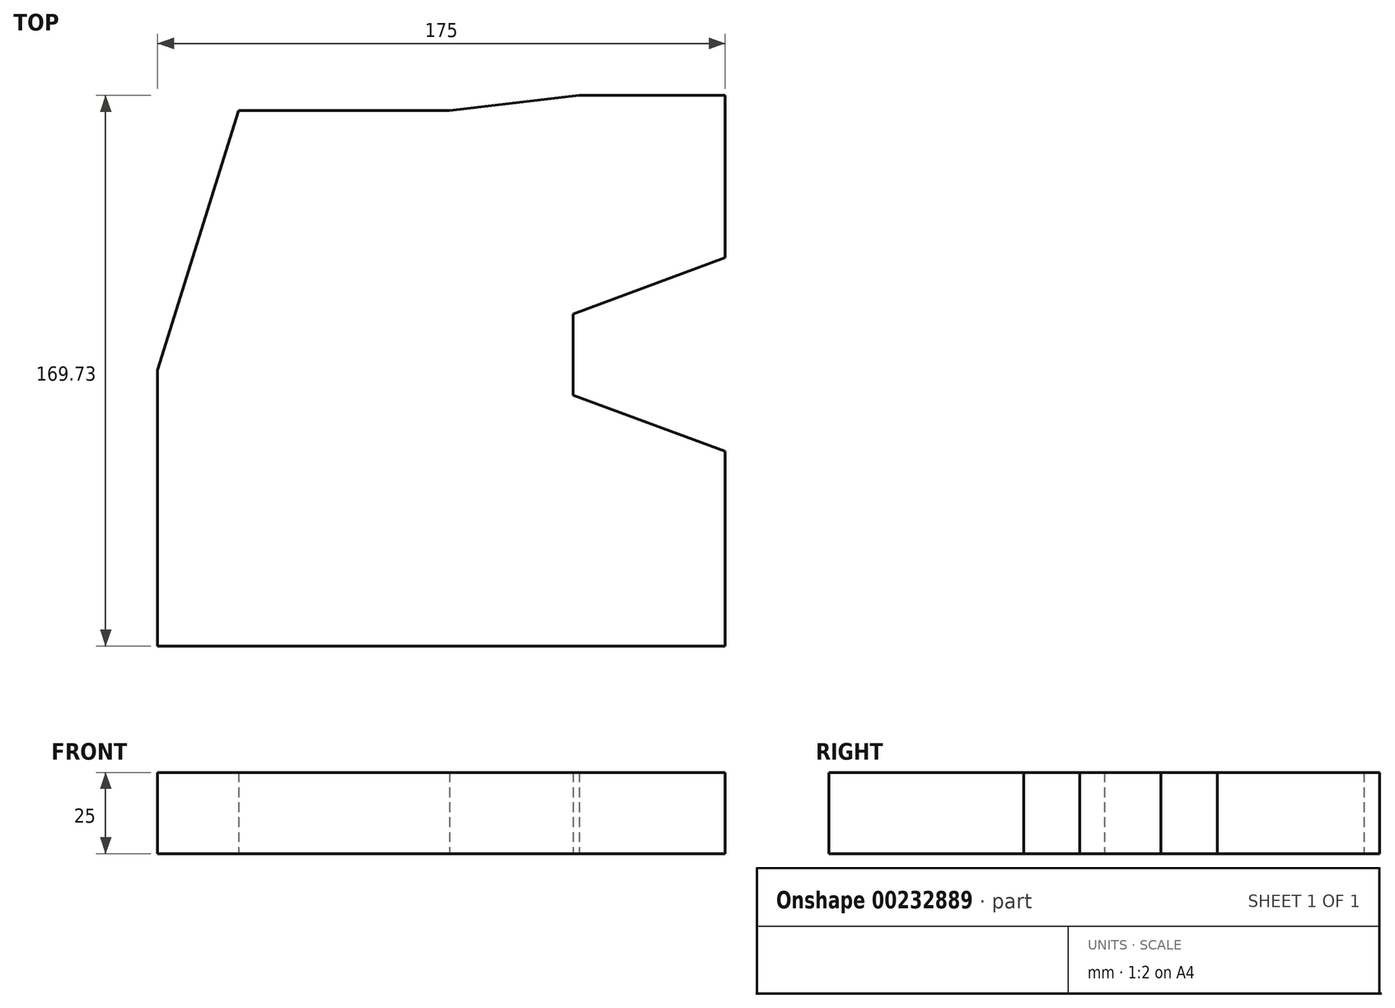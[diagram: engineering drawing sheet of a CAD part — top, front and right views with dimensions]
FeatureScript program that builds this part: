
annotation { "Feature Type Name" : "Feature", "Feature Type Description" : "" }
export const myFeature = defineFeature(function(context is Context, id is Id, definition is map)
    precondition{}
    {
        {
            var Q0;
            Q0=qCreatedBy(makeId("Top.planeOp"),FACE);
            var sketch = newSketch(context, id + "F0", { "sketchPlane" : qUnion([Q0])});
            skLineSegment(sketch, "E0", {"start": v(-130, -39.48) * mm, "end": v(45, -39.48) * mm});
            skLineSegment(sketch, "E1", {"start": v(45, -39.48) * mm, "end": v(45, 20.52) * mm});
            skLineSegment(sketch, "E2", {"start": v(45, 20.52) * mm, "end": v(-1.89, 37.88) * mm});
            skLineSegment(sketch, "E3", {"start": v(-1.89, 37.88) * mm, "end": v(-1.89, 62.88) * mm});
            skLineSegment(sketch, "E4", {"start": v(-1.89, 62.88) * mm, "end": v(45, 80.25) * mm});
            skLineSegment(sketch, "E5", {"start": v(45, 80.25) * mm, "end": v(45, 130.25) * mm});
            skLineSegment(sketch, "E6", {"start": v(45, 130.25) * mm, "end": v(0, 130.25) * mm});
            skLineSegment(sketch, "E7", {"start": v(0, 130.25) * mm, "end": v(-40, 125.52) * mm});
            skLineSegment(sketch, "E8", {"start": v(-40, 125.52) * mm, "end": v(-105, 125.52) * mm});
            skLineSegment(sketch, "E9", {"start": v(-130, -39.48) * mm, "end": v(-130, 45.52) * mm});
            skLineSegment(sketch, "E10", {"start": v(-105, 125.52) * mm, "end": v(-130, 45.52) * mm});
            skSolve(sketch);
        }
        {
            var Q0;
            Q0 = qSketchRegion(id + "F0", true);
            extrude(context, id + "F1", {"entities" : qUnion([Q0]), "depth" : 25 * mm});
        }
    });
